# Revit family: 36-8X-116 DN25-50
name_source: partatom
category: Pipe Accessories
units: mm (PartAtom-declared; Revit-internal decimal feet)

## family parameters
Always vertical = Yes
Cut with Voids When Loaded = No
Part Type = Valve - Breaks Into
Round Connector Dimension = Use Diameter
Shared = No
Work Plane-Based = No

## types (4) — shared parameters
1 = 1 mm  [stored 0.00328084 ft]
10 = 10 mm  [stored 0.0328084 ft]
15 = 15 mm  [stored 0.0492126 ft]
6 = 6 mm  [stored 0.019685 ft]
7.5 = 8 mm  [stored 0.0262467 ft]
Bonnet_R = 13 mm  [stored 0.0426509 ft]
DN025_PN16 = 36-032-80-16306499
DN032_PN16 = 36-040-80-16306499
 36-040-80-16306499
  36-040-80-16306499
DN040_PN16 = 36-050-80-163
DN050_PN16 = 36-063-80-163
Description_ = AVK SERVICE CONNECTION VALVE, DI, PN16
F = 6 mm  [stored 0.019685 ft]
F1 = 9 mm  [stored 0.0295276 ft]
F11 = 11 mm
F2 = 35 mm  [stored 0.114829 ft]
F22 = 8 mm  [stored 0.0262467 ft]
F3 = 13 mm  [stored 0.0426509 ft]
F4 = 16 mm  [stored 0.0524934 ft]
F5 = 30 mm  [stored 0.0984252 ft]
L1 = 300 mm
L2 = 24 mm  [stored 0.0787402 ft]
L3 = 315 mm
Search_table = 36-8X-116 DN25-50
URL_product_pages = https://www.avkvalves.com
zero-valued in all types: 0, Default Elevation

## per-type parameters (varying)
- DN025_PN16: Body_H=56 mm; Body_L=31 mm; Body_L1=34 mm; Body_L2=40 mm  [stored 0.131234 ft]; Body_L3=24 mm  [stored 0.0787402 ft]; Body_Rib_L=8 mm  [stored 0.0262467 ft]; Body_T=20 mm  [stored 0.0656168 ft]; Body_W=26 mm; Body_rib1=34 mm; Bore=13 mm  [stored 0.0426509 ft]; CD_H=28 mm  [stored 0.0918635 ft]; CD_L=38 mm  [stored 0.124672 ft]; Connection_D=22 mm; D=16 mm  [stored 0.0524934 ft]; D1=18 mm  [stored 0.0590551 ft]; D2=21 mm; DN=25 mm  [stored 0.082021 ft]; F6=31 mm; H=163 mm; H3=190 mm; H3-H=27 mm  [stored 0.0885827 ft]; L=400 mm; Rib_L=25 mm  [stored 0.082021 ft]; Thickness=7 mm  [stored 0.0229659 ft]; W=36 mm  [stored 0.11811 ft]; bonnet_L=102 mm; bonnet_W=71 mm
- DN032_PN16: Body_H=69 mm; Body_L=31 mm; Body_L1=34 mm; Body_L2=40 mm  [stored 0.131234 ft]; Body_L3=24 mm  [stored 0.0787402 ft]; Body_Rib_L=10 mm  [stored 0.0328084 ft]; Body_T=20 mm  [stored 0.0656168 ft]; Body_W=26 mm; Body_rib1=34 mm; Bore=16 mm  [stored 0.0524934 ft]; CD_H=35 mm  [stored 0.114829 ft]; CD_L=38 mm  [stored 0.124672 ft]; Connection_D=29 mm  [stored 0.0951444 ft]; D=20 mm  [stored 0.0656168 ft]; D1=23 mm  [stored 0.0754593 ft]; D2=26 mm; DN=32 mm  [stored 0.104987 ft]; F6=31 mm; H=176 mm; H3=209 mm; H3-H=33 mm  [stored 0.108268 ft]; L=425 mm; Rib_L=25 mm  [stored 0.082021 ft]; Thickness=7 mm  [stored 0.0229659 ft]; W=36 mm  [stored 0.11811 ft]; bonnet_L=102 mm; bonnet_W=71 mm
- DN040_PN16: Body_H=99 mm; Body_L=44 mm; Body_L1=48 mm; Body_L2=57 mm  [stored 0.187008 ft]; Body_L3=35 mm  [stored 0.114829 ft]; Body_Rib_L=13 mm  [stored 0.0426509 ft]; Body_T=29 mm  [stored 0.0951444 ft]; Body_W=38 mm  [stored 0.124672 ft]; Body_rib1=48 mm; Bore=20 mm  [stored 0.0656168 ft]; CD_H=44 mm; CD_L=45 mm  [stored 0.147638 ft]; Connection_D=30 mm  [stored 0.0984252 ft]; D=25 mm  [stored 0.082021 ft]; D1=29 mm  [stored 0.0951444 ft]; D2=33 mm  [stored 0.108268 ft]; DN=40 mm  [stored 0.131234 ft]; F6=44 mm; H=224 mm; H3=260 mm; H3-H=36 mm  [stored 0.11811 ft]; L=425 mm; Rib_L=36 mm  [stored 0.11811 ft]; Thickness=10 mm  [stored 0.0328084 ft]; W=45 mm  [stored 0.147638 ft]; bonnet_L=125 mm; bonnet_W=90 mm
- DN050_PN16: Body_H=110 mm; Body_L=44 mm; Body_L1=48 mm; Body_L2=57 mm  [stored 0.187008 ft]; Body_L3=35 mm  [stored 0.114829 ft]; Body_Rib_L=16 mm  [stored 0.0524934 ft]; Body_T=30 mm  [stored 0.0984252 ft]; Body_W=38 mm  [stored 0.124672 ft]; Body_rib1=48 mm; Bore=25 mm  [stored 0.082021 ft]; CD_H=55 mm  [stored 0.180446 ft]; CD_L=55 mm  [stored 0.180446 ft]; Connection_D=33 mm  [stored 0.108268 ft]; D=32 mm  [stored 0.104987 ft]; D1=36 mm  [stored 0.11811 ft]; D2=41 mm; DN=50 mm  [stored 0.164042 ft]; F6=44 mm; H=234 mm; H3=281 mm; H3-H=47 mm  [stored 0.154199 ft]; L=450 mm; Rib_L=36 mm  [stored 0.11811 ft]; Thickness=11 mm; W=45 mm  [stored 0.147638 ft]; bonnet_L=125 mm; bonnet_W=90 mm

note: [stored X ft] marks values corroborated as IEEE doubles in the binary element streams (Revit-internal decimal feet)

## geometry (parser evidence)
native form markers: Sweep x5
no freeform markers — native parametric forms only
